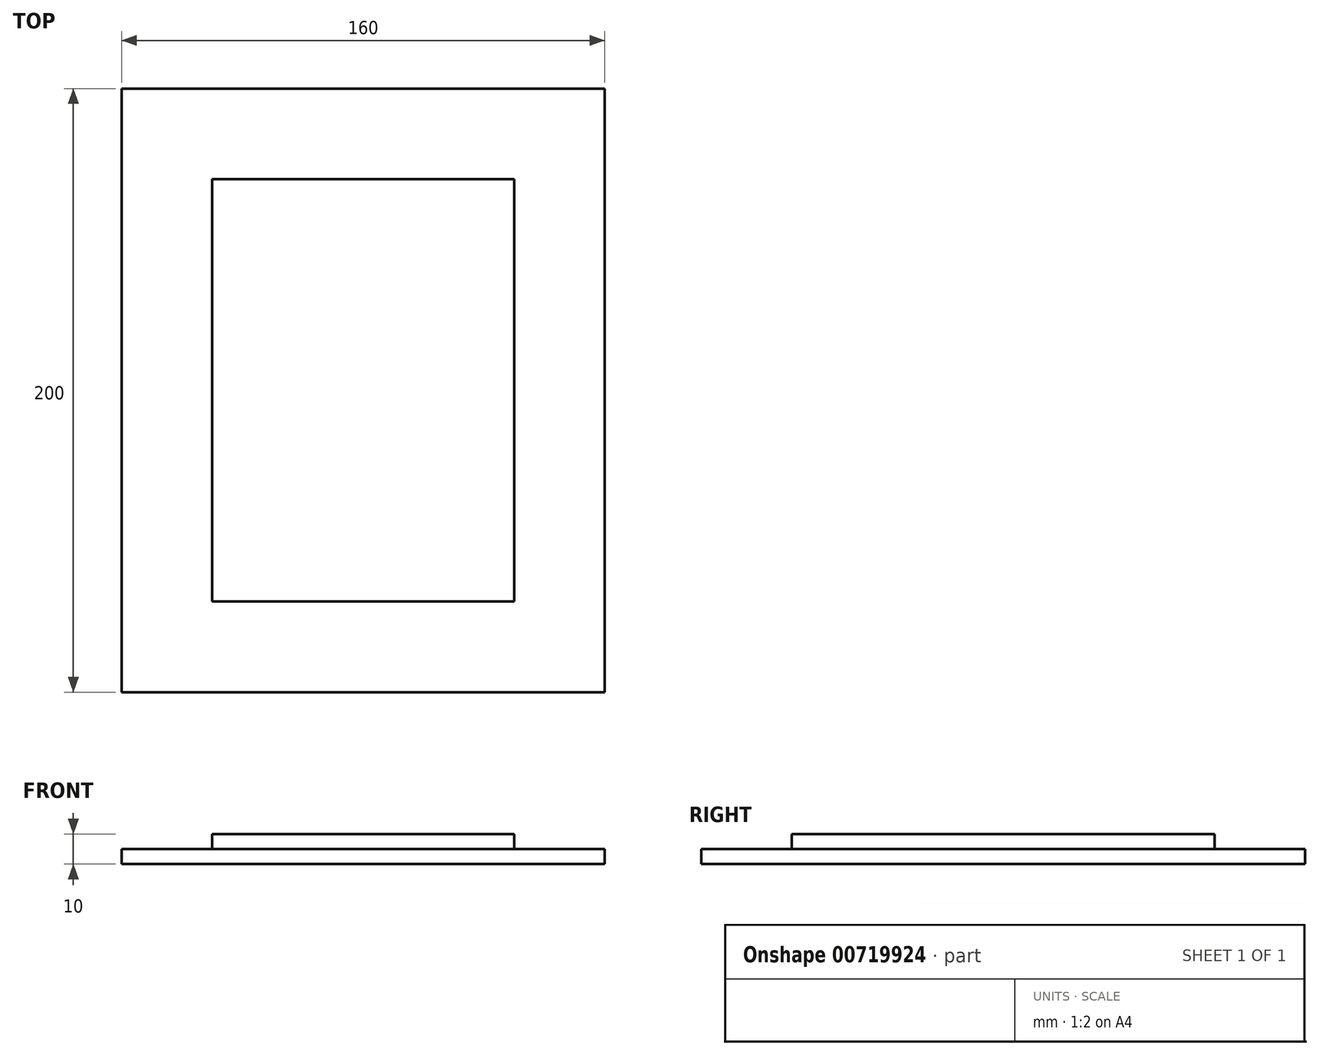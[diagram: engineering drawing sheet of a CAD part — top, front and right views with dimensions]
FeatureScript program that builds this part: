
annotation { "Feature Type Name" : "Feature", "Feature Type Description" : "" }
export const myFeature = defineFeature(function(context is Context, id is Id, definition is map)
    precondition{}
    {
        {
            var Q0;
            Q0=qCreatedBy(makeId("Top.planeOp"),FACE);
            var sketch = newSketch(context, id + "F0", { "sketchPlane" : qUnion([Q0])});
            skLineSegment(sketch, "E0.bottom", {"start": v(104.79, 165.5) * mm, "end": v(264.79, 165.5) * mm});
            skLineSegment(sketch, "E0.top", {"start": v(104.79, -34.5) * mm, "end": v(264.79, -34.5) * mm});
            skLineSegment(sketch, "E0.left", {"start": v(104.79, 165.5) * mm, "end": v(104.79, -34.5) * mm});
            skLineSegment(sketch, "E0.right", {"start": v(264.79, 165.5) * mm, "end": v(264.79, -34.5) * mm});
            skSolve(sketch);
        }
        {
            var Q0;
            Q0=makeQuery(id+"F0.imprint","IMPRINT",FACE,{"disambiguationData":[TD([[makeQuery(id+"F0.imprint","IMPRINT",EDGE,{"derivedFrom":sQuery(id+"F0.wireOp",EDGE,"E0.bottom")}),-1.0]])]});
            extrude(context, id + "F1", {"entities" : qUnion([Q0]), "depth" : 5 * mm, "offsetDistance" : 25 * mm});
        }
        {
            var Q0;
            Q0=makeQuery(id+"F1.opExtrude","CAP_FACE",FACE,{"disambiguationData":[OSD([sQuery(id+"F0.wireOp",EDGE,"E0.bottom"),sQuery(id+"F0.wireOp",EDGE,"E0.top"),sQuery(id+"F0.wireOp",EDGE,"E0.left"),sQuery(id+"F0.wireOp",EDGE,"E0.right")])],"isStart":false});
            var sketch = newSketch(context, id + "F2", { "sketchPlane" : qUnion([Q0])});
            skLineSegment(sketch, "E1.bottom", {"start": v(234.79, -4.5) * mm, "end": v(134.79, -4.5) * mm});
            skLineSegment(sketch, "E1.top", {"start": v(234.79, 135.5) * mm, "end": v(134.79, 135.5) * mm});
            skLineSegment(sketch, "E1.left", {"start": v(234.79, -4.5) * mm, "end": v(234.79, 135.5) * mm});
            skLineSegment(sketch, "E1.right", {"start": v(134.79, -4.5) * mm, "end": v(134.79, 135.5) * mm});
            skPoint(sketch, "E1.middle", {"position": v(184.79, 65.5) * mm});
            skSolve(sketch);
        }
        {
            var Q0;
            Q0=makeQuery(id+"F2.imprint","IMPRINT",FACE,{"disambiguationData":[TD([[makeQuery(id+"F2.imprint","IMPRINT",EDGE,{"derivedFrom":sQuery(id+"F2.wireOp",EDGE,"E1.bottom")}),-1.0]])]});
            extrude(context, id + "F3", {"entities" : qUnion([Q0]), "operationType" : NewBodyOperationType.ADD, "depth" : 5 * mm, "offsetDistance" : 25 * mm});
        }
    });
